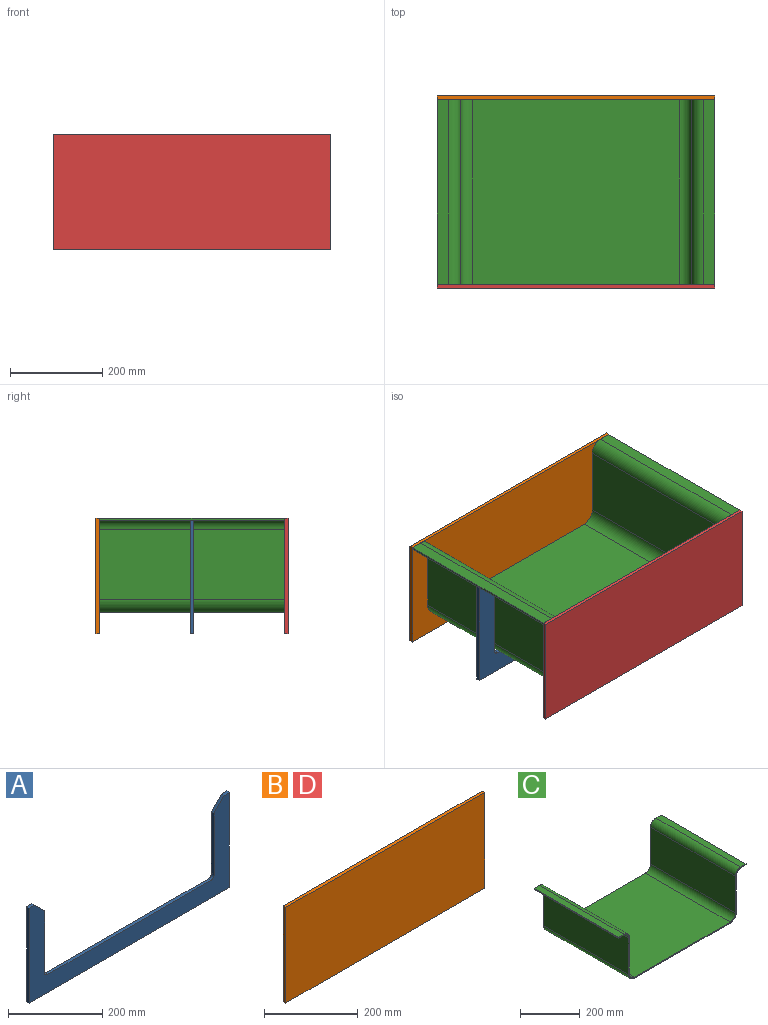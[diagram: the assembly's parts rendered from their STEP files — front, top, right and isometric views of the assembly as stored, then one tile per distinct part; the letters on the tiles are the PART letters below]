
ASSEMBLY  parts=4 mates=3
PART A: 14 faces, bbox 600x8x246 mm
  f0: plane 600x246mm, normal (0,-1,0), area 45142.9mm2, adj f2,f3,f4,f5,f6,f7,f8,f9
  f1: plane 600x246mm, normal (0,1,0), area 45142.9mm2, adj f2,f3,f4,f5,f6,f7,f8,f9
  f2: plane 246x8mm, normal (-1,0,0), area 1968mm2, adj f0,f1,f4,f5
  f3: plane 246x8mm, normal (1,0,0), area 1968mm2, adj f0,f1,f4,f9
  f4: plane 600x8mm, normal (0,0,-1), area 4800mm2, adj f0,f1,f2,f3
  f5: plane 16x8mm, normal (0,0,1), area 128mm2, adj f0,f1,f2,f10
  f6: plane 160x8mm, normal (1,0,0), area 1280mm2, adj f0,f1,f10,f12
  f7: plane 488x8mm, normal (0,0,1), area 3904mm2, adj f0,f1,f12,f13
  f8: plane 160x8mm, normal (-1,0,0), area 1280mm2, adj f0,f1,f11,f13
  f9: plane 16x8mm, normal (0,0,1), area 128mm2, adj f0,f1,f3,f11
  f10: plane 30x30mm, normal (0.71,0,0.71), area 339.4mm2, adj f0,f1,f5,f6
  f11: plane 30x30mm, normal (-0.71,0,0.71), area 339.4mm2, adj f0,f1,f8,f9
  f12: cylinder r=10mm len=10mm, axis (0,1,0), area 125.7mm2, adj f0,f1,f6,f7
  f13: cylinder r=10mm len=10mm, axis (0,1,0), area 125.7mm2, adj f0,f1,f7,f8
PART B: 6 faces, bbox 600x8x250 mm
  f0: plane 250x8mm, normal (-1,0,0), area 2000mm2, adj f2,f3,f4,f5
  f1: plane 250x8mm, normal (1,0,0), area 2000mm2, adj f2,f3,f4,f5
  f2: plane 600x8mm, normal (0,0,1), area 4800mm2, adj f0,f1,f3,f4
  f3: plane 600x250mm, normal (0,-1,0), area 150000mm2, adj f0,f1,f2,f5
  f4: plane 600x250mm, normal (0,1,0), area 150000mm2, adj f0,f1,f2,f5
  f5: plane 600x8mm, normal (0,0,-1), area 4800mm2, adj f0,f1,f3,f4
PART C: 22 faces, bbox 600x400x204 mm
  f0: plane 400x4mm, normal (1,0,0), area 1600mm2, adj f1,f3,f8,f17
  f1: plane 600x204mm, normal (0,-1,0), area 3828.3mm2, adj f0,f2,f4,f5,f6,f7,f8,f9
  f2: plane 400x4mm, normal (-1,0,0), area 1600mm2, adj f1,f3,f4,f13
  f3: plane 600x204mm, normal (0,1,0), area 3828.3mm2, adj f0,f2,f4,f5,f6,f7,f8,f9
  f4: plane 400x25mm, normal (0,0,-1), area 10000mm2, adj f1,f2,f3,f9
  f5: plane 400x150mm, normal (-1,0,0), area 60000mm2, adj f1,f3,f9,f10
  f6: plane 450x400mm, normal (0,0,-1), area 180000mm2, adj f1,f3,f10,f11
  f7: plane 400x150mm, normal (1,0,0), area 60000mm2, adj f1,f3,f11,f12
  f8: plane 400x25mm, normal (0,0,-1), area 10000mm2, adj f0,f1,f3,f12
  f9: cylinder r=21mm len=400mm, axis (0,-1,0), area 13194.7mm2, adj f1,f3,f4,f5
  f10: cylinder r=29mm len=400mm, axis (0,1,0), area 18221.2mm2, adj f1,f3,f5,f6
  f11: cylinder r=29mm len=400mm, axis (0,1,0), area 18221.2mm2, adj f1,f3,f6,f7
  f12: cylinder r=21mm len=400mm, axis (0,-1,0), area 13194.7mm2, adj f1,f3,f7,f8
  f13: plane 400x25mm, normal (0,0,1), area 10000mm2, adj f1,f2,f3,f18
  f14: plane 400x150mm, normal (1,0,0), area 60000mm2, adj f1,f3,f18,f19
  f15: plane 450x400mm, normal (0,0,1), area 180000mm2, adj f1,f3,f19,f20
  f16: plane 400x150mm, normal (-1,0,0), area 60000mm2, adj f1,f3,f20,f21
  f17: plane 400x25mm, normal (0,0,1), area 10000mm2, adj f0,f1,f3,f21
  f18: cylinder r=25mm len=400mm, axis (0,-1,0), area 15708mm2, adj f1,f3,f13,f14
  f19: cylinder r=25mm len=400mm, axis (0,1,0), area 15708mm2, adj f1,f3,f14,f15
  f20: cylinder r=25mm len=400mm, axis (0,1,0), area 15708mm2, adj f1,f3,f15,f16
  f21: cylinder r=25mm len=400mm, axis (0,-1,0), area 15708mm2, adj f1,f3,f16,f17
PART D: same geometry as B
PLACE A t=(0,4,0)mm
PLACE B t=(0,408,0)mm
PLACE C at identity fixed
PLACE D at identity
MATE fastened A.f9 <-> C.f8  axis (0,0,1) through (550,200,196)mm
MATE fastened B.f3 <-> C.f3  axis (0,-1,0) through (550,400,200)mm
MATE fastened D.f4 <-> C.f1  axis (0,1,0) through (550,0,200)mm
